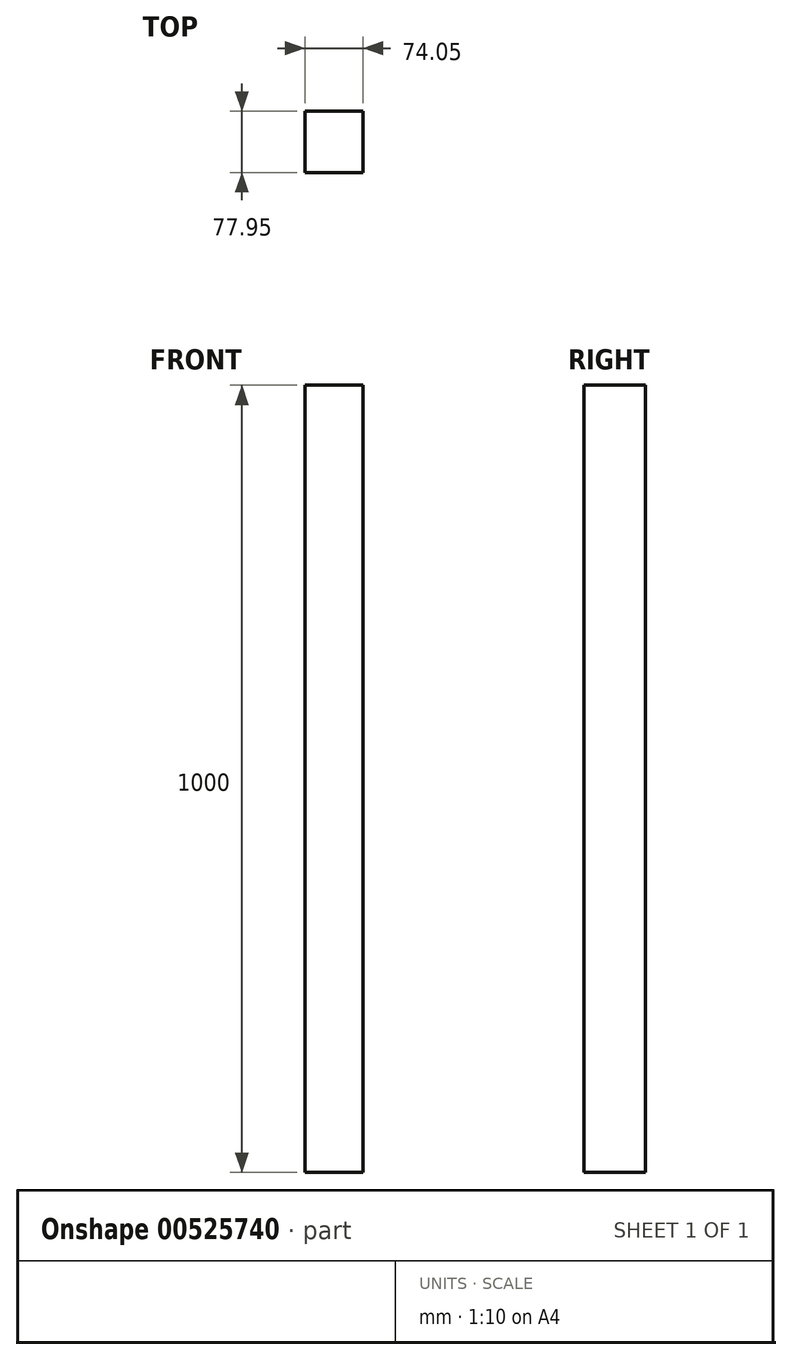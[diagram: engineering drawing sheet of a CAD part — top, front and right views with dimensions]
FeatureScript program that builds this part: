
annotation { "Feature Type Name" : "Feature", "Feature Type Description" : "" }
export const myFeature = defineFeature(function(context is Context, id is Id, definition is map)
    precondition{}
    {
        {
            var Q0;
            Q0=qCreatedBy(makeId("Top.planeOp"),FACE);
            var sketch = newSketch(context, id + "F0", { "sketchPlane" : qUnion([Q0])});
            skLineSegment(sketch, "E0.bottom", {"start": v(-34.21, 35.51) * mm, "end": v(39.84, 35.51) * mm});
            skLineSegment(sketch, "E0.top", {"start": v(-34.21, -42.44) * mm, "end": v(39.84, -42.44) * mm});
            skLineSegment(sketch, "E0.left", {"start": v(-34.21, 35.51) * mm, "end": v(-34.21, -42.44) * mm});
            skLineSegment(sketch, "E0.right", {"start": v(39.84, 35.51) * mm, "end": v(39.84, -42.44) * mm});
            skSolve(sketch);
        }
        {
            var Q0;
            Q0=makeQuery(id+"F0.imprint","IMPRINT",FACE,{"disambiguationData":[TD([[makeQuery(id+"F0.imprint","IMPRINT",EDGE,{"derivedFrom":sQuery(id+"F0.wireOp",EDGE,"E0.bottom")}),-1.0]])]});
            extrude(context, id + "F1", {"entities" : qUnion([Q0]), "depth" : 1000 * mm, "offsetDistance" : 25 * mm});
        }
    });
